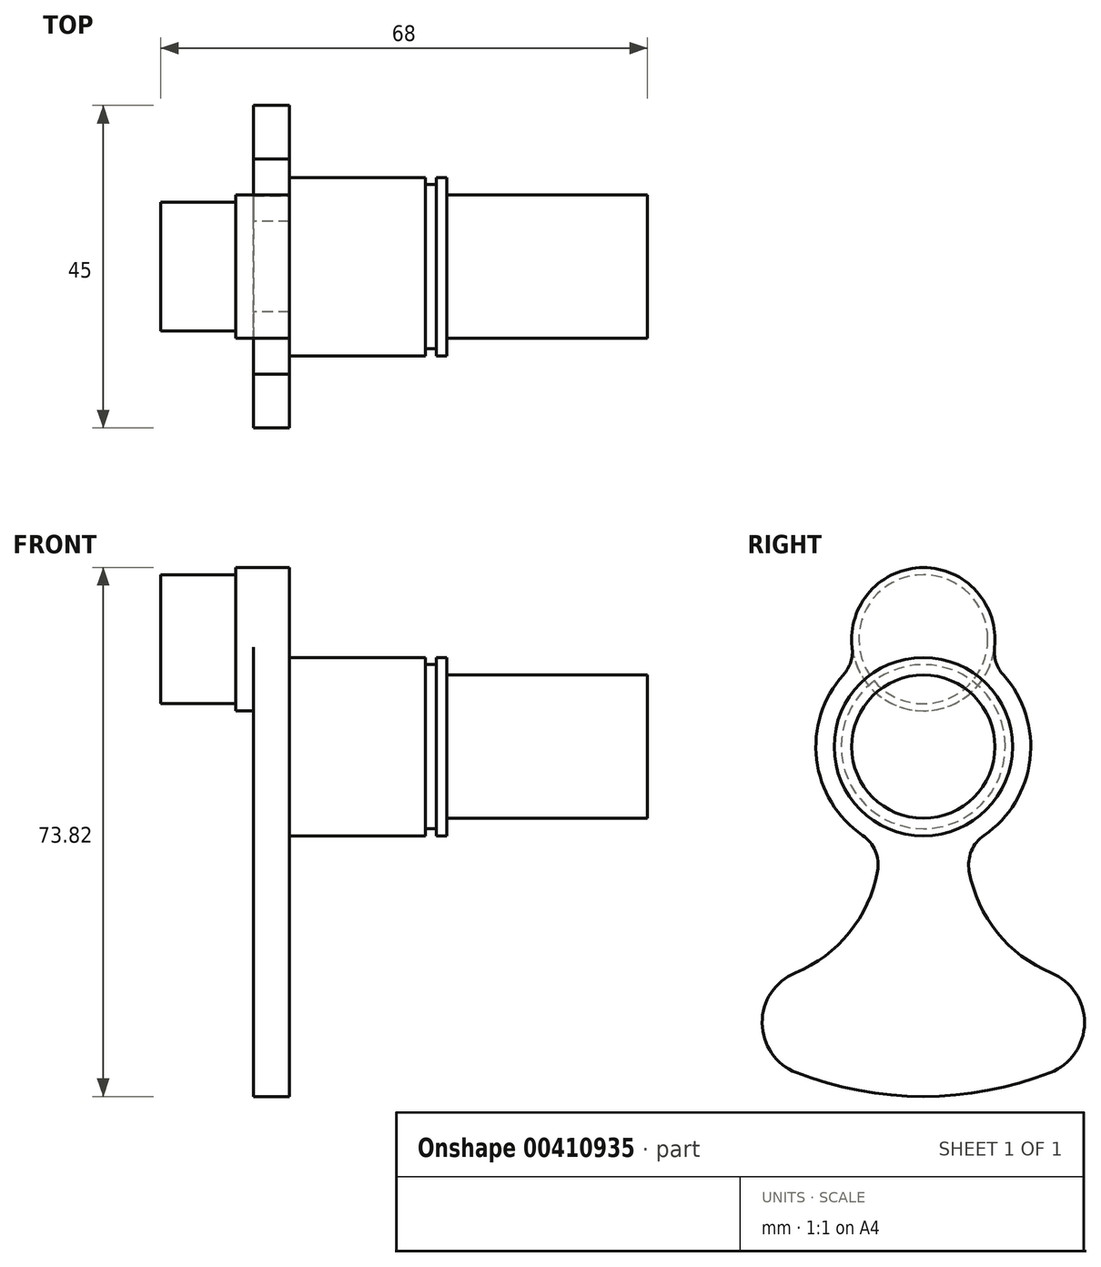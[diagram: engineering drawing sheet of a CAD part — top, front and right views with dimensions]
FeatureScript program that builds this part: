
annotation { "Feature Type Name" : "Feature", "Feature Type Description" : "" }
export const myFeature = defineFeature(function(context is Context, id is Id, definition is map)
    precondition{}
    {
        {
            var Q0;
            Q0=qCreatedBy(makeId("Right.planeOp"),FACE);
            var sketch = newSketch(context, id + "F0", { "sketchPlane" : qUnion([Q0])});
            skArc(sketch, "E0", {"start": v(-17.86, -31.57) * mm, "mid": v(-22.5, -38.57) * mm, "end": v(-17.72, -45.49) * mm});
            skArc(sketch, "E1", {"start": v(17.72, -45.49) * mm, "mid": v(22.5, -38.57) * mm, "end": v(17.86, -31.57) * mm});
            skArc(sketch, "E2", {"start": v(-9.43, 11.67) * mm, "mid": v(-14.87, -1.95) * mm, "end": v(-6.1, -13.7) * mm});
            skArc(sketch, "E3", {"start": v(9.43, 11.67) * mm, "mid": v(0, 25) * mm, "end": v(-9.43, 11.67) * mm});
            skArc(sketch, "E4.trimOffspring", {"start": v(6.1, -13.7) * mm, "mid": v(14.87, -1.95) * mm, "end": v(9.43, 11.67) * mm});
            skArc(sketch, "E5", {"start": v(-17.72, -45.49) * mm, "mid": v(0, -48.82) * mm, "end": v(17.72, -45.49) * mm});
            skArc(sketch, "E6", {"start": v(-17.86, -31.57) * mm, "mid": v(-9.23, -24.45) * mm, "end": v(-6.1, -13.7) * mm});
            skArc(sketch, "E7", {"start": v(6.1, -13.7) * mm, "mid": v(9.23, -24.45) * mm, "end": v(17.86, -31.57) * mm});
            skSolve(sketch);
        }
        {
            var Q0;
            Q0=makeQuery(id+"F0.imprint","IMPRINT",FACE,{"disambiguationData":[TD([[makeQuery(id+"F0.imprint","IMPRINT",EDGE,{"derivedFrom":sQuery(id+"F0.wireOp",EDGE,"E0")}),1.0]])]});
            extrude(context, id + "F1", {"entities" : qUnion([Q0]), "depth" : 5 * mm});
        }
        {
            var Q0;
            Q0=qCreatedBy(makeId("Front.planeOp"),FACE);
            var sketch = newSketch(context, id + "F2", { "sketchPlane" : qUnion([Q0])});
            skLineSegment(sketch, "E8.bottom", {"start": v(5, 12.45) * mm, "end": v(24, 12.45) * mm});
            skLineSegment(sketch, "E8.top", {"start": v(5, 0) * mm, "end": v(55, 0) * mm});
            skLineSegment(sketch, "E8.left", {"start": v(5, 12.45) * mm, "end": v(5, 0) * mm});
            skLineSegment(sketch, "E8.right", {"start": v(27, 12.45) * mm, "end": v(27, 10) * mm});
            skLineSegment(sketch, "E9.top", {"start": v(24, 11.45) * mm, "end": v(25.5, 11.45) * mm});
            skLineSegment(sketch, "E9.left", {"start": v(24, 12.45) * mm, "end": v(24, 11.45) * mm});
            skLineSegment(sketch, "E9.right", {"start": v(25.5, 12.45) * mm, "end": v(25.5, 11.45) * mm});
            skLineSegment(sketch, "E10.bottom", {"start": v(27, 10) * mm, "end": v(55, 10) * mm});
            skLineSegment(sketch, "E10.right", {"start": v(55, 10) * mm, "end": v(55, 0) * mm});
            skLineSegment(sketch, "E11.trimOffspring", {"start": v(25.5, 12.45) * mm, "end": v(27, 12.45) * mm});
            skSolve(sketch);
        }
        {
            var Q0;
            Q0 = qSketchRegion(id + "F2", true);
            var Q1;
            Q1=sQuery(id+"F2.wireOp",EDGE,"E8.top");
            revolve(context, id + "F3", {"operationType" : NewBodyOperationType.ADD, "entities" : qUnion([Q0]), "axis" : qUnion([Q1]), "revolveType" : RevolveType.FULL});
        }
        {
            var Q0;
            Q0=makeQuery(id+"F1.opExtrude","SWEPT_EDGE",EDGE,{"disambiguationData":[OSD([sQuery(id+"F0.wireOp",EDGE,"E2"),sQuery(id+"F0.wireOp",EDGE,"E3")])]});
            var Q1;
            Q1=makeQuery(id+"F1.opExtrude","SWEPT_EDGE",EDGE,{"disambiguationData":[OSD([sQuery(id+"F0.wireOp",EDGE,"E2"),sQuery(id+"F0.wireOp",EDGE,"E6")])]});
            var Q2;
            Q2=makeQuery(id+"F1.opExtrude","SWEPT_EDGE",EDGE,{"disambiguationData":[OSD([sQuery(id+"F0.wireOp",EDGE,"E3"),sQuery(id+"F0.wireOp",EDGE,"E4.trimOffspring")])]});
            var Q3;
            Q3=makeQuery(id+"F1.opExtrude","SWEPT_EDGE",EDGE,{"disambiguationData":[OSD([sQuery(id+"F0.wireOp",EDGE,"E4.trimOffspring"),sQuery(id+"F0.wireOp",EDGE,"E7")])]});
            fillet(context, id + "F4", {"entities" : qUnion([Q0, Q1, Q2, Q3]), "radius" : 5 * mm, "tangentPropagation" : true, "allowEdgeOverflow" : false});
        }
        {
            var Q0;
            Q0=qCreatedBy(makeId("Front.planeOp"),FACE);
            var sketch = newSketch(context, id + "F5", { "sketchPlane" : qUnion([Q0])});
            skLineSegment(sketch, "E12.bottom", {"start": v(-2.5, 25) * mm, "end": v(0, 25) * mm});
            skLineSegment(sketch, "E12.top", {"start": v(-13, 15) * mm, "end": v(0, 15) * mm});
            skLineSegment(sketch, "E12.left", {"start": v(-13, 24) * mm, "end": v(-13, 15) * mm});
            skLineSegment(sketch, "E12.right", {"start": v(0, 25) * mm, "end": v(0, 15) * mm});
            skLineSegment(sketch, "E13.top", {"start": v(-13, 24) * mm, "end": v(-2.5, 24) * mm});
            skLineSegment(sketch, "E13.right", {"start": v(-2.5, 25) * mm, "end": v(-2.5, 24) * mm});
            skSolve(sketch);
        }
        {
            var Q0;
            Q0 = qSketchRegion(id + "F5", true);
            var Q1;
            Q1=sQuery(id+"F5.wireOp",EDGE,"E12.top");
            revolve(context, id + "F6", {"operationType" : NewBodyOperationType.ADD, "entities" : qUnion([Q0]), "axis" : qUnion([Q1]), "revolveType" : RevolveType.FULL});
        }
    });
